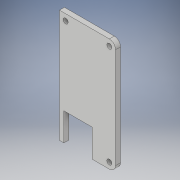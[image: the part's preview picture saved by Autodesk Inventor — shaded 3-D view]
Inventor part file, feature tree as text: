
AUTODESK INVENTOR PART (.ipt)
format: ipt  version: 2019 (Build 230136000, 136)  size: 121,856 bytes
history: native  units: in
note: dims shown in document units (in); Inventor stores cm internally (conversion verified against a paired STEP export)
features: sketch x2, extrude x1, hole x1
ambient origin geometry x8: Origin, YZ Plane, XZ Plane, XY Plane, X Axis, Y Axis, Z Axis, Center Point
bodies: Solid1 (feature_tree)
feature tree (4):
  extrude  "Scanner Cover"  Depth=0.1in TaperAngle=0.0deg
  hole  "Screw Holes"  [1 undecoded]
  sketch  "Sketch1"  dims[d1=2.27in d5=0.1in d6=0.0in]
  sketch  "Sketch2"  dims[d7=0.125in d8=0.125in d9=0.125in d10=0.125in d11=0.47in d12=1.13in d13=0.125in d14=0.1in d15=0.75in d16=0.375in d17=0.25in d18=0.5635in d19=1.0in d20=0.8108in d21=0.56in d22=0.125in d23=0.125in d24=0.09in]
note: 1 required parameter value undecoded (feature->parameter linkage not recoverable at this tier; creation-order binding heuristic only, values carry confidence <= 0.55)
